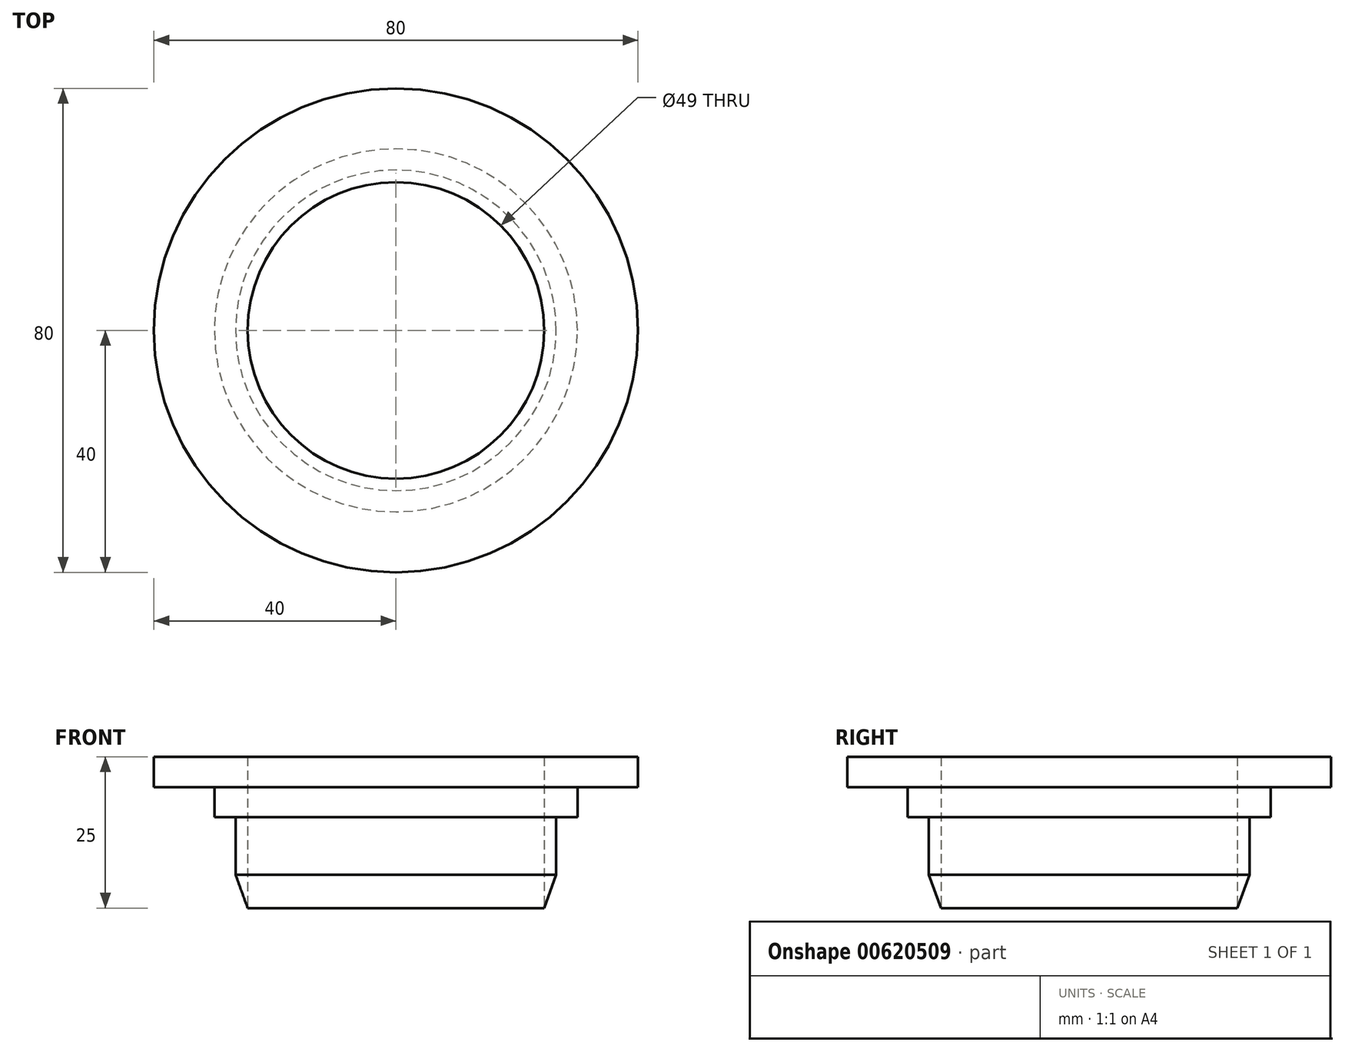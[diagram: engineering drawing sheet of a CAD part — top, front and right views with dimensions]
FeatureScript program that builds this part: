
annotation { "Feature Type Name" : "Feature", "Feature Type Description" : "" }
export const myFeature = defineFeature(function(context is Context, id is Id, definition is map)
    precondition{}
    {
        {
            var Q0;
            Q0=qCreatedBy(makeId("Front.planeOp"),FACE);
            var sketch = newSketch(context, id + "F0", { "sketchPlane" : qUnion([Q0])});
            skLineSegment(sketch, "E0", {"start": v(-24.5, 0) * mm, "end": v(-24.5, 25) * mm});
            skLineSegment(sketch, "E1", {"start": v(-24.5, 25) * mm, "end": v(-40, 25) * mm});
            skLineSegment(sketch, "E2", {"start": v(-40, 25) * mm, "end": v(-40, 20) * mm});
            skLineSegment(sketch, "E3", {"start": v(-26.5, 5.5) * mm, "end": v(-24.5, 0) * mm});
            skLineSegment(sketch, "E4", {"start": v(-40, 20) * mm, "end": v(-30, 20) * mm});
            skLineSegment(sketch, "E5", {"start": v(-30, 20) * mm, "end": v(-30, 15) * mm});
            skLineSegment(sketch, "E6", {"start": v(-30, 15) * mm, "end": v(-26.5, 15) * mm});
            skLineSegment(sketch, "E7", {"start": v(-26.5, 15) * mm, "end": v(-26.5, 5.5) * mm});
            skLineSegment(sketch, "E8", {"start": v(0, 0) * mm, "end": v(0, 47.42) * mm, "construction": true});
            skSolve(sketch);
        }
        {
            var Q0;
            Q0=makeQuery(id+"F0.imprint","IMPRINT",FACE,{"disambiguationData":[TD([[makeQuery(id+"F0.imprint","IMPRINT",EDGE,{"derivedFrom":sQuery(id+"F0.wireOp",EDGE,"E0")}),1.0]])]});
            var Q1;
            Q1=sQuery(id+"F0.wireOp",EDGE,"E8");
            revolve(context, id + "F1", {"entities" : qUnion([Q0]), "axis" : qUnion([Q1]), "revolveType" : RevolveType.FULL});
        }
    });
